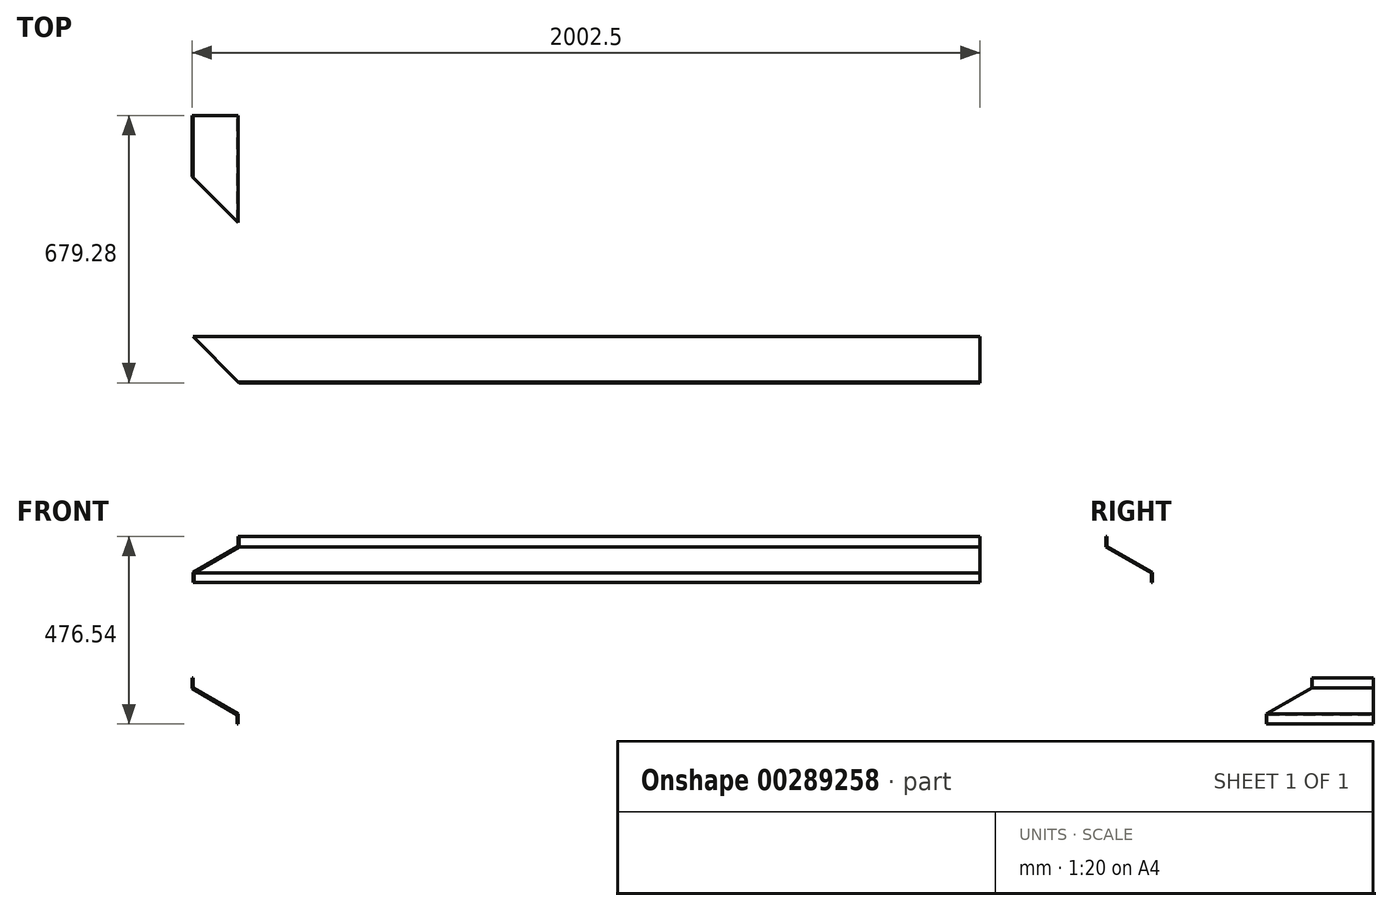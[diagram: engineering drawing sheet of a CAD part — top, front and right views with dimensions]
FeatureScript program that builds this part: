
annotation { "Feature Type Name" : "Feature", "Feature Type Description" : "" }
export const myFeature = defineFeature(function(context is Context, id is Id, definition is map)
    precondition{}
    {
        {
            var Q0;
            Q0=qCreatedBy(makeId("Front.planeOp"),FACE);
            var sketch = newSketch(context, id + "F0", { "sketchPlane" : qUnion([Q0])});
            skLineSegment(sketch, "E0", {"start": v(0, 0) * mm, "end": v(0, -25) * mm});
            skLineSegment(sketch, "E1", {"start": v(0, -25) * mm, "end": v(115, -91.4) * mm});
            skLineSegment(sketch, "E2", {"start": v(115, -91.4) * mm, "end": v(115, -116.4) * mm});
            skLineSegment(sketch, "E3", {"start": v(0, 0) * mm, "end": v(-2.5, 0) * mm});
            skLineSegment(sketch, "E4", {"start": v(-2.5, 0) * mm, "end": v(-2.5, -26.44) * mm});
            skLineSegment(sketch, "E5", {"start": v(-2.5, -26.44) * mm, "end": v(112.5, -92.84) * mm});
            skLineSegment(sketch, "E6", {"start": v(112.5, -92.84) * mm, "end": v(112.5, -116.4) * mm});
            skLineSegment(sketch, "E7", {"start": v(112.5, -116.4) * mm, "end": v(115, -116.4) * mm});
            skSolve(sketch);
        }
        {
            var Q0;
            Q0=makeQuery(id+"F0.imprint","IMPRINT",FACE,{"disambiguationData":[TD([[makeQuery(id+"F0.imprint","IMPRINT",EDGE,{"derivedFrom":sQuery(id+"F0.wireOp",EDGE,"E0")}),-1.0]])]});
            extrude(context, id + "F1", {"entities" : qUnion([Q0]), "depth" : 252 * mm + 20 * mm});
        }
        {
            var Q0;
            Q0=makeQuery(id+"F1.opExtrude","SWEPT_FACE",FACE,{"disambiguationData":[OSD([sQuery(id+"F0.wireOp",EDGE,"E7")])]});
            var sketch = newSketch(context, id + "F2", { "sketchPlane" : qUnion([Q0])});
            skLineSegment(sketch, "E8", {"start": v(115, 272) * mm, "end": v(-2.5, 154.5) * mm});
            skLineSegment(sketch, "E9", {"start": v(112.5, 272) * mm, "end": v(-2.5, 272) * mm});
            skLineSegment(sketch, "E10.0", {"start": v(-2.5, 272) * mm, "end": v(-2.5, 0) * mm});
            skLineSegment(sketch, "E11", {"start": v(112.5, 272) * mm, "end": v(115, 272) * mm});
            skSolve(sketch);
        }
        {
            var Q0;
            {var subQ6=sQuery(id+"F2.wireOp",EDGE,"E9");Q0=makeQuery(id+"F2.imprint","IMPRINT",FACE,{"disambiguationData":[TD([[makeQuery(id+"F2.imprint","IMPRINT",EDGE,{"derivedFrom":subQ6}),1.0]])]});}
            extrude(context, id + "F3", {"entities" : qUnion([Q0]), "operationType" : NewBodyOperationType.REMOVE, "endBound" : BoundingType.THROUGH_ALL, "oppositeDirection" : true, "depth" : 25 * mm});
        }
        {
            var Q0;
            Q0=qCreatedBy(makeId("Right.planeOp"),FACE);
            var sketch = newSketch(context, id + "F4", { "sketchPlane" : qUnion([Q0])});
            skLineSegment(sketch, "E12", {"start": v(-676.78, 360.14) * mm, "end": v(-676.78, 335.14) * mm});
            skLineSegment(sketch, "E13", {"start": v(-676.78, 335.14) * mm, "end": v(-561.78, 268.75) * mm});
            skLineSegment(sketch, "E14", {"start": v(-561.78, 268.75) * mm, "end": v(-561.78, 243.75) * mm});
            skLineSegment(sketch, "E15", {"start": v(-676.78, 360.14) * mm, "end": v(-679.28, 360.14) * mm});
            skLineSegment(sketch, "E16", {"start": v(-679.28, 360.14) * mm, "end": v(-679.28, 333.7) * mm});
            skLineSegment(sketch, "E17", {"start": v(-679.28, 333.7) * mm, "end": v(-564.28, 267.3) * mm});
            skLineSegment(sketch, "E18", {"start": v(-564.28, 267.3) * mm, "end": v(-564.28, 243.75) * mm});
            skLineSegment(sketch, "E19", {"start": v(-564.28, 243.75) * mm, "end": v(-561.78, 243.75) * mm});
            skSolve(sketch);
        }
        {
            var Q0;
            Q0=makeQuery(id+"F4.imprint","IMPRINT",FACE,{"disambiguationData":[TD([[makeQuery(id+"F4.imprint","IMPRINT",EDGE,{"derivedFrom":sQuery(id+"F4.wireOp",EDGE,"E12")}),-1.0]])]});
            extrude(context, id + "F5", {"entities" : qUnion([Q0]), "depth" : 2000 * mm});
        }
        {
            var Q0;
            Q0=makeQuery(id+"F1.opExtrude","SWEPT_FACE",FACE,{"disambiguationData":[OSD([sQuery(id+"F0.wireOp",EDGE,"E7")])]});
            var sketch = newSketch(context, id + "F6", { "sketchPlane" : qUnion([Q0])});
            skLineSegment(sketch, "E20", {"start": v(115, 272) * mm, "end": v(112.5, 269.5) * mm});
            skLineSegment(sketch, "E21", {"start": v(112.5, 269.5) * mm, "end": v(112.5, 272) * mm});
            skLineSegment(sketch, "E22", {"start": v(112.5, 272) * mm, "end": v(115, 272) * mm});
            skSolve(sketch);
        }
        {
            var Q0;
            Q0=makeQuery(id+"F6.imprint","IMPRINT",FACE,{"disambiguationData":[TD([[makeQuery(id+"F6.imprint","IMPRINT",EDGE,{"derivedFrom":sQuery(id+"F6.wireOp",EDGE,"E20")}),-1.0]])]});
            extrude(context, id + "F7", {"entities" : qUnion([Q0]), "operationType" : NewBodyOperationType.REMOVE, "endBound" : BoundingType.THROUGH_ALL, "oppositeDirection" : true, "depth" : 25 * mm});
        }
        {
            var Q0;
            Q0=makeQuery(id+"F5.opExtrude","SWEPT_FACE",FACE,{"disambiguationData":[OSD([sQuery(id+"F4.wireOp",EDGE,"E19")])]});
            var sketch = newSketch(context, id + "F8", { "sketchPlane" : qUnion([Q0])});
            skLineSegment(sketch, "E23", {"start": v(0, 561.78) * mm, "end": v(117.5, 679.28) * mm});
            skLineSegment(sketch, "E24.0", {"start": v(117.5, 679.28) * mm, "end": v(0, 679.28) * mm});
            skLineSegment(sketch, "E25.0", {"start": v(0, 676.78) * mm, "end": v(0, 679.28) * mm});
            skLineSegment(sketch, "E26.0", {"start": v(0, 679.28) * mm, "end": v(0, 564.28) * mm});
            skLineSegment(sketch, "E27.0", {"start": v(0, 564.28) * mm, "end": v(0, 561.78) * mm});
            skPoint(sketch, "E28.orphan", {"position": v(2000, 679.28) * mm});
            skSolve(sketch);
        }
        {
            var Q0;
            {var subQ0=sQuery(id+"F8.wireOp",EDGE,"E24.0");Q0=makeQuery(id+"F8.imprint","IMPRINT",FACE,{"disambiguationData":[TD([[makeQuery(id+"F8.imprint","IMPRINT",EDGE,{"derivedFrom":subQ0}),1.0]])]});}
            var Q1;
            {var subQ0=sQuery(id+"F8.wireOp",EDGE,"E27.0");Q1=makeQuery(id+"F8.imprint","IMPRINT",FACE,{"disambiguationData":[TD([[makeQuery(id+"F8.imprint","IMPRINT",EDGE,{"derivedFrom":subQ0}),1.0]])]});}
            extrude(context, id + "F9", {"entities" : qUnion([Q0, Q1]), "operationType" : NewBodyOperationType.REMOVE, "endBound" : BoundingType.THROUGH_ALL, "oppositeDirection" : true, "depth" : 25 * mm});
        }
        {
            var Q0;
            Q0=makeQuery(id+"F1.opExtrude","SWEPT_BODY",BODY,{"disambiguationData":[OSD([sQuery(id+"F0.wireOp",EDGE,"E0"),sQuery(id+"F0.wireOp",EDGE,"E1"),sQuery(id+"F0.wireOp",EDGE,"E2"),sQuery(id+"F0.wireOp",EDGE,"E3"),sQuery(id+"F0.wireOp",EDGE,"E4"),sQuery(id+"F0.wireOp",EDGE,"E5"),sQuery(id+"F0.wireOp",EDGE,"E6"),sQuery(id+"F0.wireOp",EDGE,"E7")])]});
            transform(context, id + "F10", {"entities" : qUnion([Q0]), "transformType" : TransformType.TRANSLATION_3D, "dx" : 0 * mm, "dy" : 0 * mm, "dz" : 0 * mm, "makeCopy" : true});
        }
        {
            var Q0;
            Q0=makeQuery(id+"F10.opPattern","COPY",BODY,{"derivedFrom":makeQuery(id+"F1.opExtrude","SWEPT_BODY",BODY,{"disambiguationData":[OSD([sQuery(id+"F0.wireOp",EDGE,"E0"),sQuery(id+"F0.wireOp",EDGE,"E1"),sQuery(id+"F0.wireOp",EDGE,"E2"),sQuery(id+"F0.wireOp",EDGE,"E3"),sQuery(id+"F0.wireOp",EDGE,"E4"),sQuery(id+"F0.wireOp",EDGE,"E5"),sQuery(id+"F0.wireOp",EDGE,"E6"),sQuery(id+"F0.wireOp",EDGE,"E7")])]}),"instanceName":"1"});
            deleteBodies(context, id + "F11", {"entities" : qUnion([Q0])});
        }
    });
